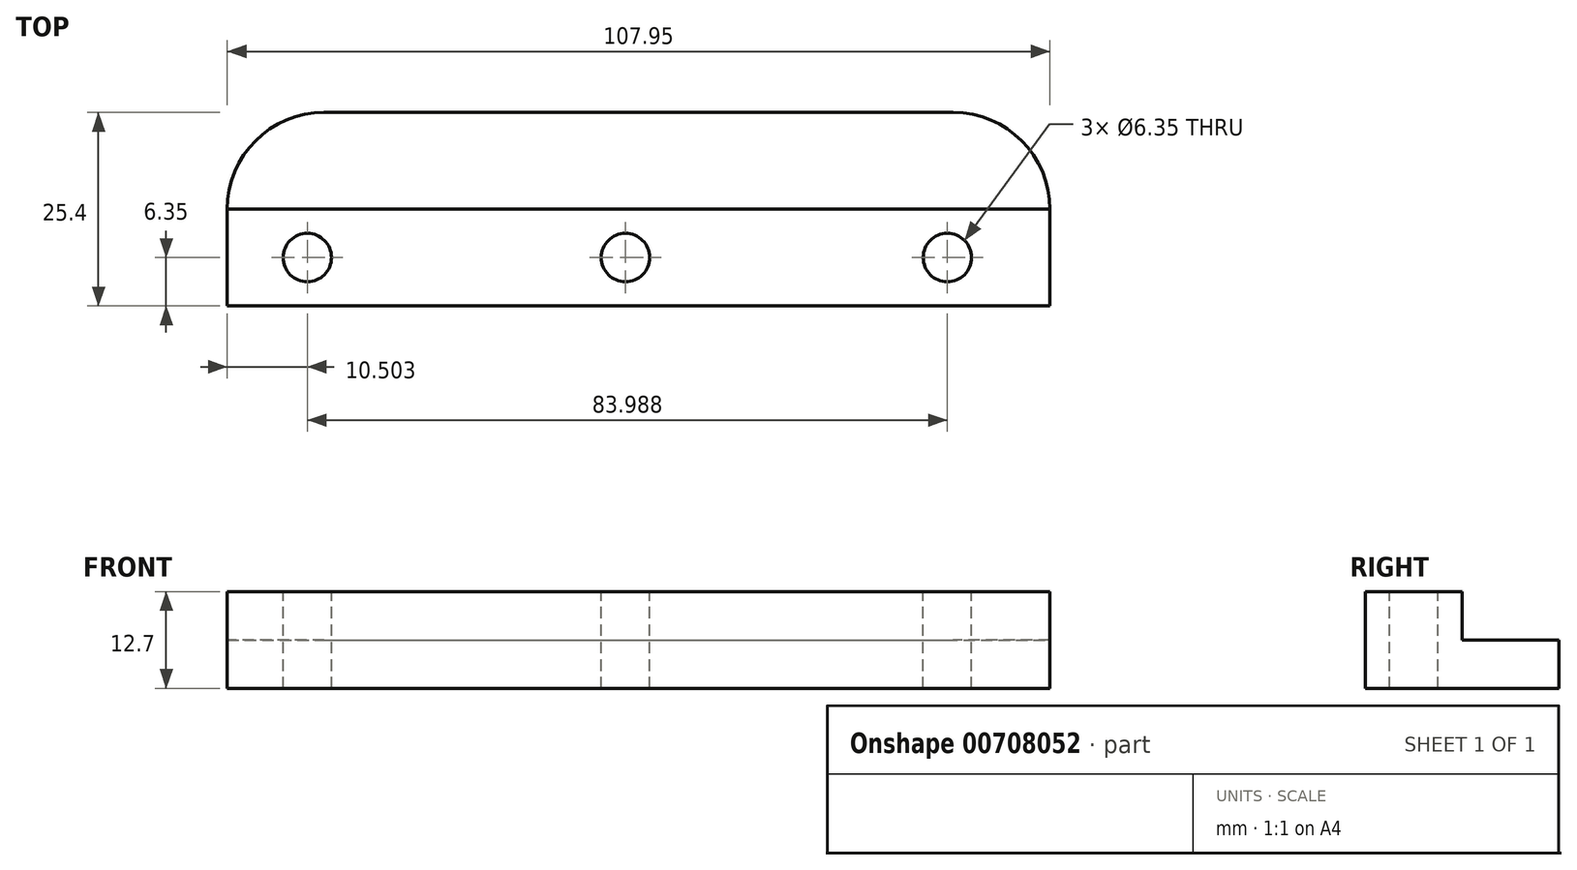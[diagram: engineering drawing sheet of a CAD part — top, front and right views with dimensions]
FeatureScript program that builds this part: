
annotation { "Feature Type Name" : "Feature", "Feature Type Description" : "" }
export const myFeature = defineFeature(function(context is Context, id is Id, definition is map)
    precondition{}
    {
        {
            var Q0;
            Q0=qCreatedBy(makeId("Top.planeOp"),FACE);
            var sketch = newSketch(context, id + "F0", { "sketchPlane" : qUnion([Q0])});
            skLineSegment(sketch, "E0.bottom", {"start": v(0, 0) * mm, "end": v(107.95, 0) * mm});
            skLineSegment(sketch, "E0.top", {"start": v(12.7, 25.4) * mm, "end": v(95.25, 25.4) * mm});
            skLineSegment(sketch, "E0.left", {"start": v(0, 0) * mm, "end": v(0, 12.7) * mm});
            skLineSegment(sketch, "E0.right", {"start": v(107.95, 0) * mm, "end": v(107.95, 12.7) * mm});
            skPoint(sketch, "E1.visualSharp", {"position": v(0, 25.4) * mm});
            skArc(sketch, "E1.filletArc", {"start": v(12.7, 25.4) * mm, "mid": v(3.72, 21.68) * mm, "end": v(0, 12.7) * mm});
            skPoint(sketch, "E2.visualSharp", {"position": v(107.95, 25.4) * mm});
            skArc(sketch, "E2.filletArc", {"start": v(107.95, 12.7) * mm, "mid": v(104.23, 21.68) * mm, "end": v(95.25, 25.4) * mm});
            skSolve(sketch);
        }
        {
            var Q0;
            Q0=makeQuery(id+"F0.imprint","IMPRINT",FACE,{"disambiguationData":[TD([[makeQuery(id+"F0.imprint","IMPRINT",EDGE,{"derivedFrom":sQuery(id+"F0.wireOp",EDGE,"E0.bottom")}),1.0]])]});
            extrude(context, id + "F1", {"entities" : qUnion([Q0]), "depth" : 6.35 * mm, "offsetDistance" : 25.4 * mm});
        }
        {
            var Q0;
            Q0=makeQuery(id+"F1.opExtrude","CAP_FACE",FACE,{"disambiguationData":[OSD([sQuery(id+"F0.wireOp",EDGE,"E0.bottom"),sQuery(id+"F0.wireOp",EDGE,"E0.top"),sQuery(id+"F0.wireOp",EDGE,"E0.left"),sQuery(id+"F0.wireOp",EDGE,"E0.right")])],"isStart":false});
            var sketch = newSketch(context, id + "F2", { "sketchPlane" : qUnion([Q0])});
            skLineSegment(sketch, "E3.bottom", {"start": v(0, 0) * mm, "end": v(107.95, 0) * mm});
            skLineSegment(sketch, "E3.top", {"start": v(0, 12.7) * mm, "end": v(107.95, 12.7) * mm});
            skLineSegment(sketch, "E3.left", {"start": v(0, 0) * mm, "end": v(0, 12.7) * mm});
            skLineSegment(sketch, "E3.right", {"start": v(107.95, 0) * mm, "end": v(107.95, 12.7) * mm});
            skSolve(sketch);
        }
        {
            var Q0;
            Q0=makeQuery(id+"F2.imprint","IMPRINT",FACE,{"disambiguationData":[TD([[makeQuery(id+"F2.imprint","IMPRINT",EDGE,{"derivedFrom":sQuery(id+"F2.wireOp",EDGE,"E3.bottom")}),1.0]])]});
            extrude(context, id + "F3", {"entities" : qUnion([Q0]), "operationType" : NewBodyOperationType.ADD, "depth" : 6.35 * mm, "offsetDistance" : 25.4 * mm});
        }
        {
            var Q0;
            Q0=makeQuery(id+"F3.opExtrude","CAP_FACE",FACE,{"disambiguationData":[OSD([sQuery(id+"F2.wireOp",EDGE,"E3.bottom"),sQuery(id+"F2.wireOp",EDGE,"E3.top"),sQuery(id+"F2.wireOp",EDGE,"E3.left"),sQuery(id+"F2.wireOp",EDGE,"E3.right")])],"isStart":false});
            var sketch = newSketch(context, id + "F4", { "sketchPlane" : qUnion([Q0])});
            skLineSegment(sketch, "E4", {"start": v(0, 6.35) * mm, "end": v(107.95, 6.35) * mm, "construction": true});
            skCircle(sketch, "E5", {"center": v(10.5, 6.35) * mm, "radius": 3.18 * mm});
            skCircle(sketch, "E6", {"center": v(52.25, 6.35) * mm, "radius": 3.18 * mm});
            skCircle(sketch, "E7", {"center": v(94.5, 6.35) * mm, "radius": 3.18 * mm});
            skSolve(sketch);
        }
        {
            var Q0;
            Q0=makeQuery(id+"F4.imprint","IMPRINT",FACE,{"disambiguationData":[TD([[makeQuery(id+"F4.imprint","IMPRINT",EDGE,{"derivedFrom":sQuery(id+"F4.wireOp",EDGE,"E5")}),1.0]])]});
            var Q1;
            Q1=makeQuery(id+"F4.imprint","IMPRINT",FACE,{"disambiguationData":[TD([[makeQuery(id+"F4.imprint","IMPRINT",EDGE,{"derivedFrom":sQuery(id+"F4.wireOp",EDGE,"E6")}),1.0]])]});
            var Q2;
            Q2=makeQuery(id+"F4.imprint","IMPRINT",FACE,{"disambiguationData":[TD([[makeQuery(id+"F4.imprint","IMPRINT",EDGE,{"derivedFrom":sQuery(id+"F4.wireOp",EDGE,"E7")}),1.0]])]});
            extrude(context, id + "F5", {"entities" : qUnion([Q0, Q1, Q2]), "operationType" : NewBodyOperationType.REMOVE, "oppositeDirection" : true, "depth" : 25.4 * mm, "offsetDistance" : 25.4 * mm});
        }
    });
